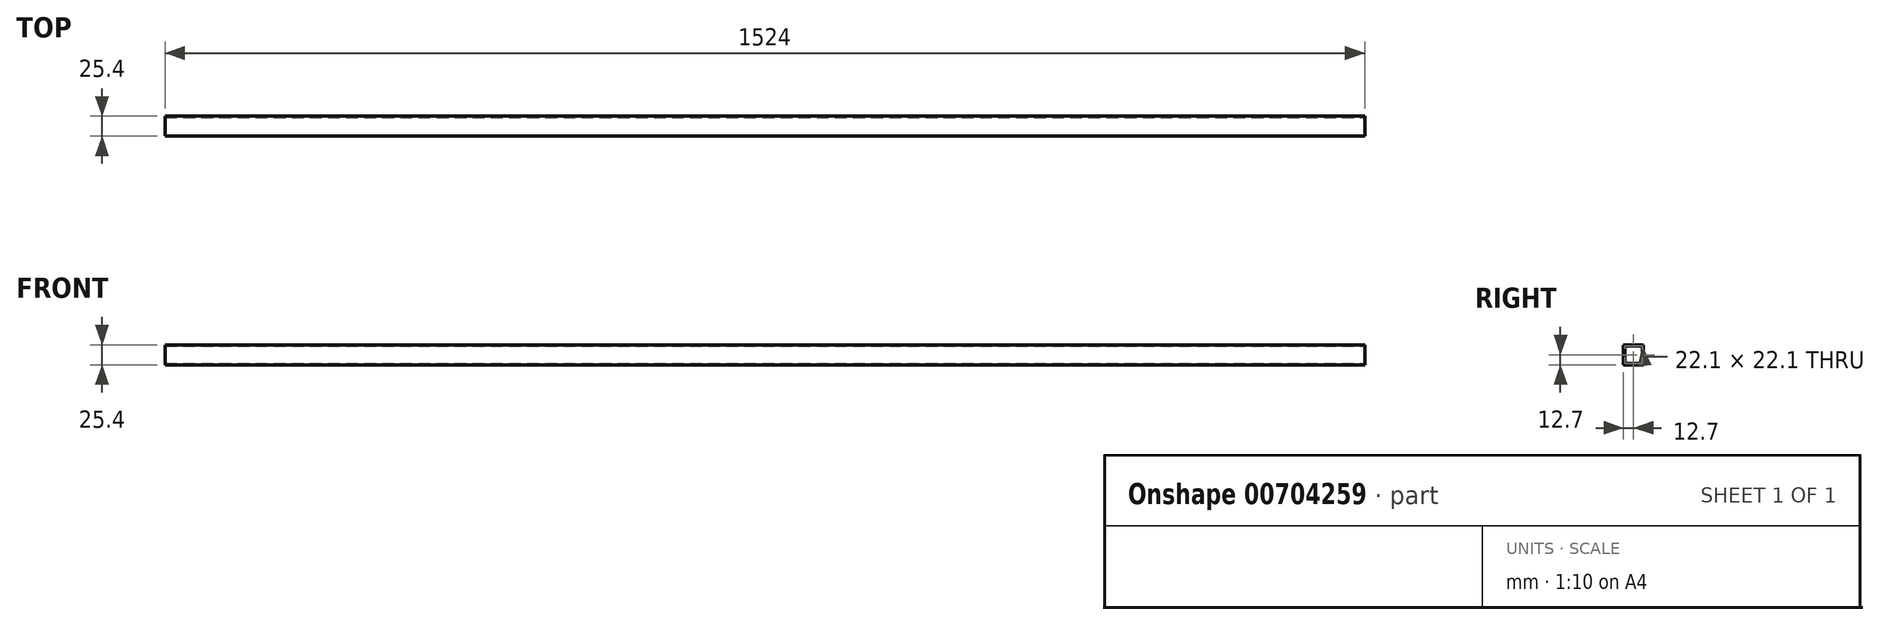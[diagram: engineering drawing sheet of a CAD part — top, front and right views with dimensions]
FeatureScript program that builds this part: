
annotation { "Feature Type Name" : "Feature", "Feature Type Description" : "" }
export const myFeature = defineFeature(function(context is Context, id is Id, definition is map)
    precondition{}
    {
        {
            var Q0;
            Q0=qCreatedBy(makeId("Front.planeOp"),FACE);
            var sketch = newSketch(context, id + "F0", { "sketchPlane" : qUnion([Q0])});
            skLineSegment(sketch, "E0.bottom", {"start": v(-762, 12.7) * mm, "end": v(762, 12.7) * mm});
            skLineSegment(sketch, "E0.top", {"start": v(-762, -12.7) * mm, "end": v(762, -12.7) * mm});
            skLineSegment(sketch, "E0.left", {"start": v(-762, 12.7) * mm, "end": v(-762, -12.7) * mm});
            skLineSegment(sketch, "E0.right", {"start": v(762, 12.7) * mm, "end": v(762, -12.7) * mm});
            skPoint(sketch, "E0.middle", {"position": v(0, 0) * mm});
            skSolve(sketch);
        }
        {
            var Q0;
            Q0=qCreatedBy(makeId("Right.planeOp"),FACE);
            var sketch = newSketch(context, id + "F1", { "sketchPlane" : qUnion([Q0])});
            skLineSegment(sketch, "E1.bottom", {"start": v(11.05, 11.05) * mm, "end": v(-11.05, 11.05) * mm});
            skLineSegment(sketch, "E1.top", {"start": v(11.05, -11.05) * mm, "end": v(-11.05, -11.05) * mm});
            skLineSegment(sketch, "E1.left", {"start": v(11.05, 11.05) * mm, "end": v(11.05, -11.05) * mm});
            skLineSegment(sketch, "E1.right", {"start": v(-11.05, 11.05) * mm, "end": v(-11.05, -11.05) * mm});
            skPoint(sketch, "E1.middle", {"position": v(0, 0) * mm});
            skSolve(sketch);
        }
        {
            var Q0;
            Q0=makeQuery(id+"F0.imprint","IMPRINT",FACE,{"disambiguationData":[TD([[makeQuery(id+"F0.imprint","IMPRINT",EDGE,{"derivedFrom":sQuery(id+"F0.wireOp",EDGE,"E0.bottom")}),-1.0]])]});
            extrude(context, id + "F2", {"entities" : qUnion([Q0]), "endBound" : BoundingType.SYMMETRIC, "depth" : 25.4 * mm, "offsetDistance" : 25.4 * mm});
        }
        {
            var Q0;
            Q0=makeQuery(id+"F1.imprint","IMPRINT",FACE,{"disambiguationData":[TD([[makeQuery(id+"F1.imprint","IMPRINT",EDGE,{"derivedFrom":sQuery(id+"F1.wireOp",EDGE,"E1.bottom")}),1.0]])]});
            extrude(context, id + "F3", {"entities" : qUnion([Q0]), "operationType" : NewBodyOperationType.REMOVE, "endBound" : BoundingType.SYMMETRIC, "oppositeDirection" : true, "depth" : 1524 * mm, "offsetDistance" : 25.4 * mm});
        }
    });
